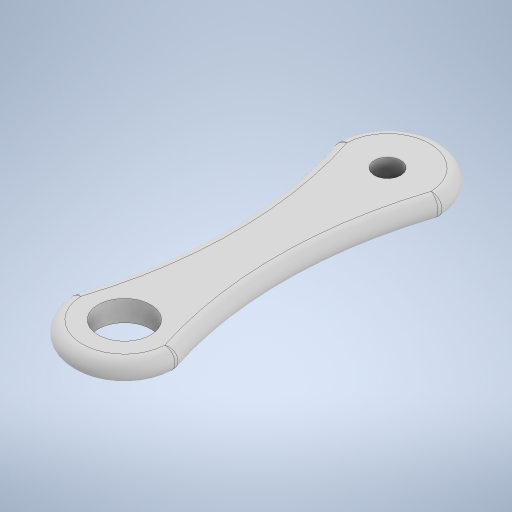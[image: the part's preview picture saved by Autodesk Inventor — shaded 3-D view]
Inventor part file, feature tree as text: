
AUTODESK INVENTOR PART (.ipt)
format: ipt  version: 2024 (Build 280153020, 153B)  size: 311,296 bytes
history: native  units: mm
features: fillet x6, extrude x5, sketch x5
ambient origin geometry x8: Origin, YZ Plane, XZ Plane, XY Plane, X Axis, Y Axis, Z Axis, Center Point
bodies: Solid1 (feature_tree)
feature tree (16):
  extrude  "Extrusion1"  Depth=4.0mm TaperAngle=0.0deg
  extrude  "Extrusion2"  Depth=4.0mm TaperAngle=0.0deg
  extrude  "Extrusion3"  Depth=4.0mm TaperAngle=0.0deg
  extrude  "Extrusion4"  Depth=2.0mm
  fillet  "Fillet1"  Radius=2.0mm
  fillet  "Fillet2"  Radius=2.0mm
  fillet  "Fillet3"  Radius=5.0mm
  fillet  "Fillet4"  Radius=4.0mm
  extrude  "Extrusion5"  Depth=2.0mm
  fillet  "Fillet5"  Radius=20.0mm
  fillet  "Fillet6"  [1 undecoded]
  sketch  "Sketch1"  dims[d0=20.0mm d1=4.0mm d2=0.0mm]
  sketch  "Sketch2"  dims[d3=50.0mm d4=4.0mm d5=0.0mm]
  sketch  "Sketch3"  dims[d6=4.0mm d7=0.0mm d8=4.0mm d9=0.0mm]
  sketch  "Sketch5"  dims[d10=2.0mm d11=2.0mm d12=2.0mm d13=2.0mm d14=5.0mm d15=4.0mm d16=0.0mm]
  sketch  "Sketch6"  dims[d17=2.0mm d18=2.0mm d19=20.0mm]
note: 1 required parameter value undecoded (feature->parameter linkage not recoverable at this tier; creation-order binding heuristic only, values carry confidence <= 0.55)
